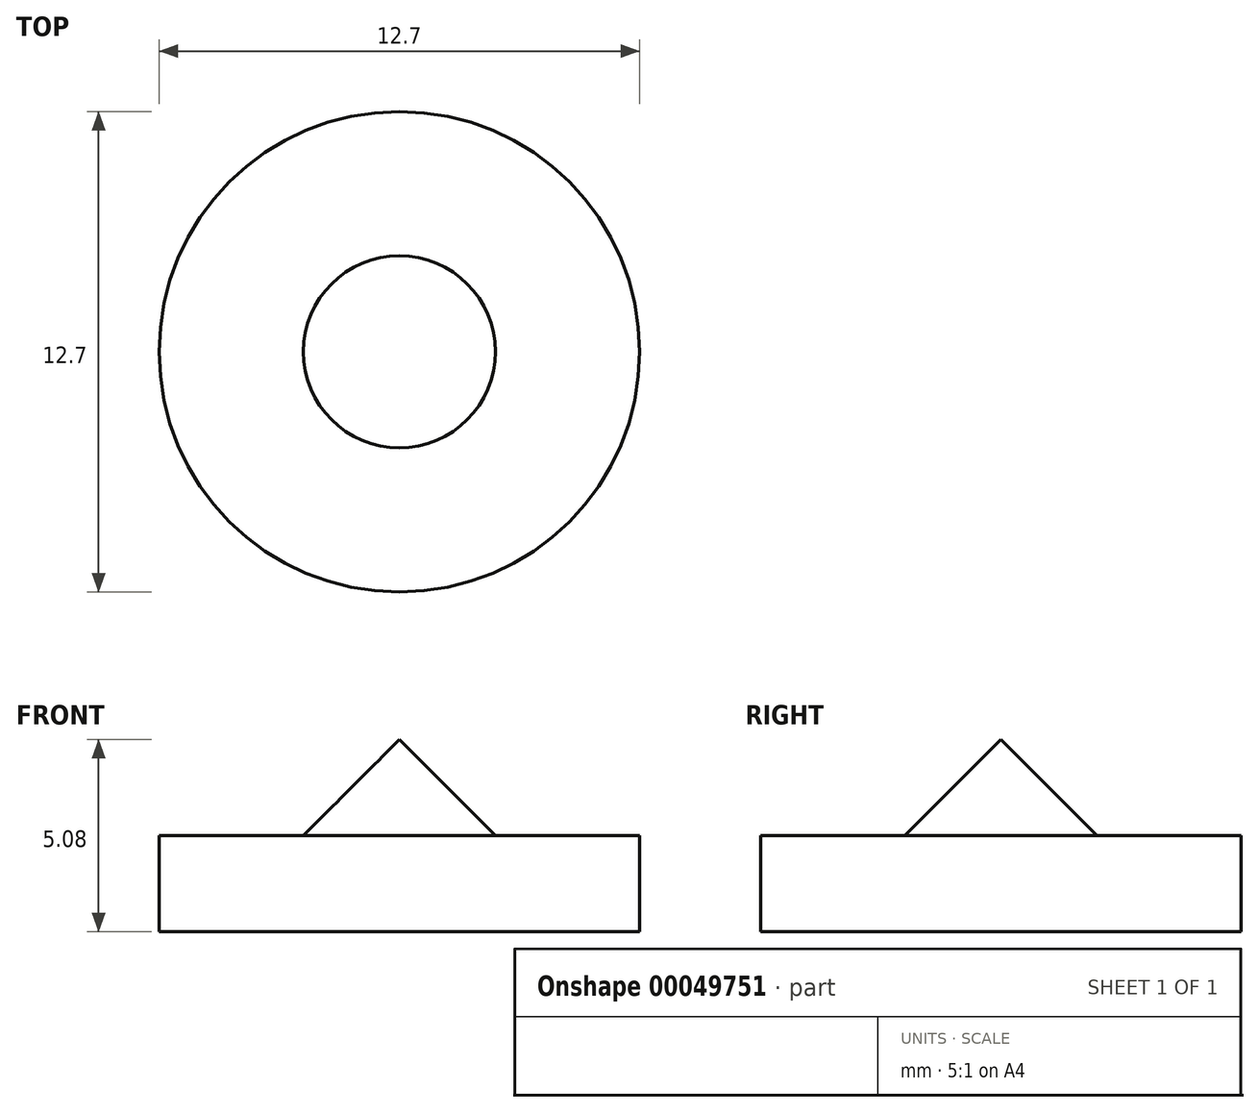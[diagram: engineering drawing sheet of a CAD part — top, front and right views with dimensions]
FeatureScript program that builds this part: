
annotation { "Feature Type Name" : "Feature", "Feature Type Description" : "" }
export const myFeature = defineFeature(function(context is Context, id is Id, definition is map)
    precondition{}
    {
        {
            var Q0;
            Q0=qCreatedBy(makeId("Top.planeOp"),FACE);
            var sketch = newSketch(context, id + "F0", { "sketchPlane" : qUnion([Q0])});
            skCircle(sketch, "E0", {"center": v(0, 0) * mm, "radius": 6.35 * mm});
            skSolve(sketch);
        }
        {
            var Q0;
            Q0=qCreatedBy(makeId("Top.planeOp"),FACE);
            var sketch = newSketch(context, id + "F1", { "sketchPlane" : qUnion([Q0])});
            skCircle(sketch, "E1", {"center": v(0, 0) * mm, "radius": 2.54 * mm});
            skSolve(sketch);
        }
        {
            var Q0;
            Q0=makeQuery(id+"F1.imprint","IMPRINT",FACE,{"disambiguationData":[TD([[makeQuery(id+"F1.imprint","IMPRINT",EDGE,{"derivedFrom":sQuery(id+"F1.wireOp",EDGE,"E1")}),1.0]])]});
            cPlane(context, id + "F2", {"entities" : qUnion([Q0]), "cplaneType" : CPlaneType.OFFSET, "offset" : 2.54 * mm, "width" : 152.4 * mm, "height" : 152.4 * mm});
        }
        {
            var Q0;
            Q0=qCreatedBy(id+"F2.planeOp",FACE);
            var sketch = newSketch(context, id + "F3", { "sketchPlane" : qUnion([Q0])});
            skPoint(sketch, "E2", {"position": v(0, 0) * mm});
            skSolve(sketch);
        }
        {
            var Q0;
            Q0=sQuery(id+"F3.wireOp",VERTEX,"E2");
            var Q1;
            Q1=makeQuery(id+"F1.imprint","IMPRINT",FACE,{"disambiguationData":[TD([[makeQuery(id+"F1.imprint","IMPRINT",EDGE,{"derivedFrom":sQuery(id+"F1.wireOp",EDGE,"E1")}),1.0]])]});
            loft(context, id + "F4", {"sheetProfilesArray" : [{ "sheetProfileEntities" : qUnion([Q0]) }, { "sheetProfileEntities" : qUnion([Q1]) }]});
        }
        {
            var Q0;
            Q0=makeQuery(id+"F0.imprint","IMPRINT",FACE,{"disambiguationData":[TD([[makeQuery(id+"F0.imprint","IMPRINT",EDGE,{"derivedFrom":sQuery(id+"F0.wireOp",EDGE,"E0")}),1.0]])]});
            extrude(context, id + "F5", {"entities" : qUnion([Q0]), "oppositeDirection" : true, "depth" : 2.54 * mm});
        }
    });
